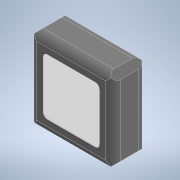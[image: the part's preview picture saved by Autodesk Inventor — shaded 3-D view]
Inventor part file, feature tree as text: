
AUTODESK INVENTOR PART (.ipt)
format: ipt  version: 2022.6 (Build 266554000, 554)  size: 166,912 bytes
history: native  units: mm
features: extrude x3, sketch x3, fillet x2, chamfer x1
ambient origin geometry x8: Origin, YZ Plane, XZ Plane, XY Plane, X Axis, Y Axis, Z Axis, Center Point
bodies: Solid1 (feature_tree)
feature tree (9):
  extrude  "Extrusion1"  Depth=40.0mm
  extrude  "Extrusion2"  Depth=2.0mm TaperAngle=45.0deg
  fillet  "Fillet1"  Radius=27.0mm
  chamfer  "Chamfer1"  Distance=0.1mm
  fillet  "Fillet2"  Radius=2.0mm
  extrude  "Extrusion3"  Depth=3.5mm
  sketch  "Sketch1"  dims[d0=40.0mm d1=40.0mm]
  sketch  "Sketch2"  dims[d2=16.0mm d3=0.0mm d4=3.0mm d5=2.0mm d6=45.0deg d7=27.0mm]
  sketch  "Sketch3"  dims[d8=27.0mm d9=0.1mm d10=0.0mm d11=2.0mm d12=3.5mm d13=8.5mm d14=2.0mm d15=0.0mm]
